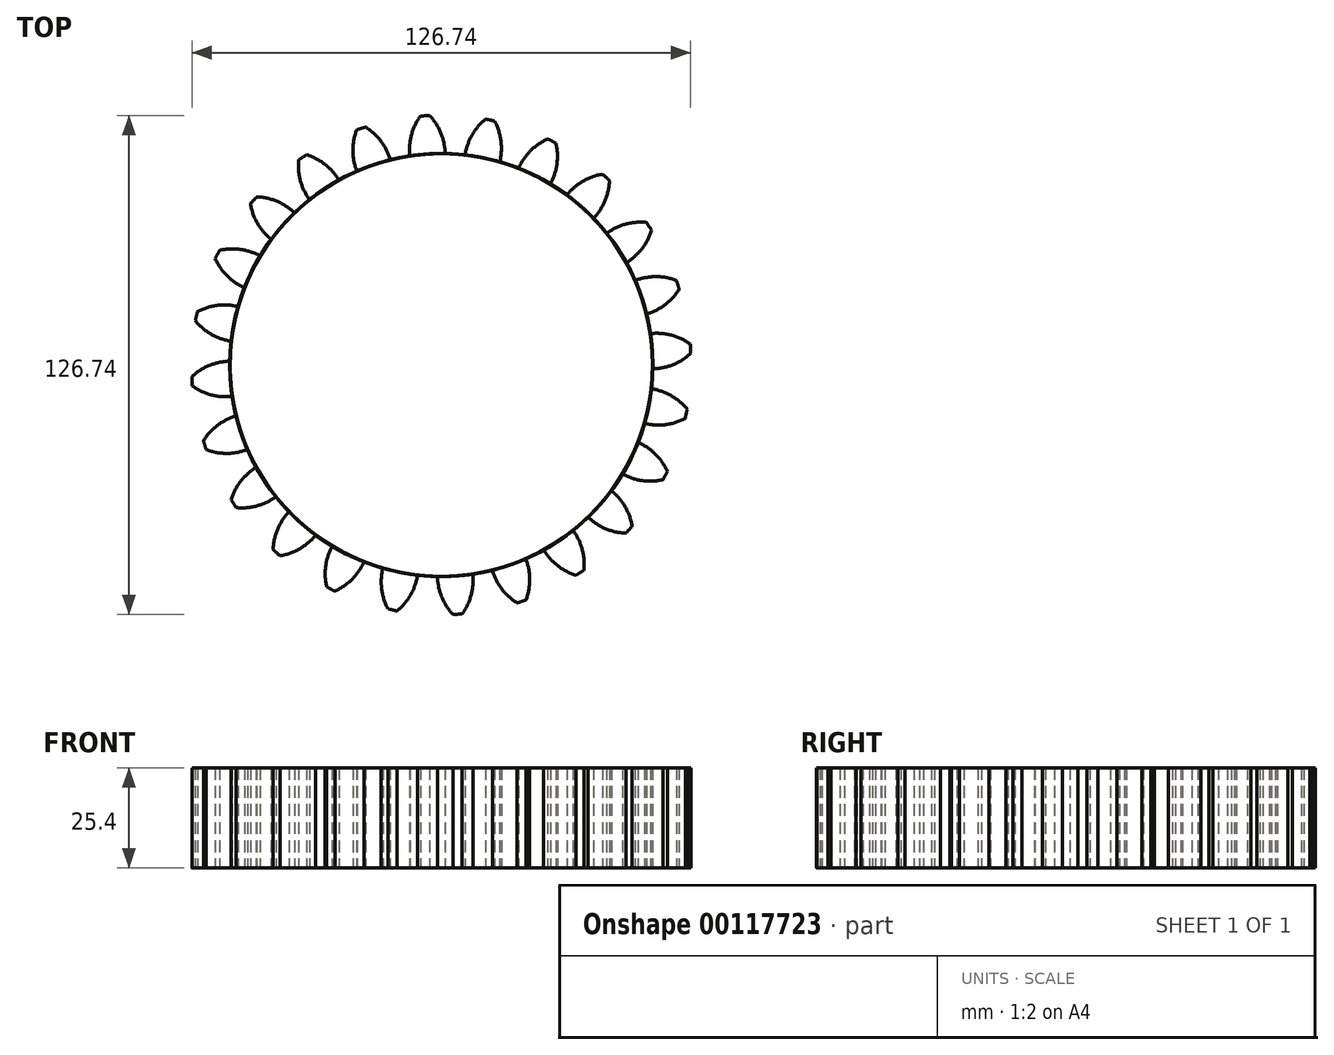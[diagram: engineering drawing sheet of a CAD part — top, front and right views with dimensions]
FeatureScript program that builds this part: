
annotation { "Feature Type Name" : "Feature", "Feature Type Description" : "" }
export const myFeature = defineFeature(function(context is Context, id is Id, definition is map)
    precondition{}
    {
        {
            var Q0;
            Q0=qCreatedBy(makeId("Top.planeOp"),FACE);
            var sketch = newSketch(context, id + "F0", { "sketchPlane" : qUnion([Q0])});
            skCircle(sketch, "E0", {"center": v(0, 0) * mm, "radius": 53.72 * mm});
            skCircle(sketch, "E1", {"center": v(0, 0) * mm, "radius": 58.67 * mm, "construction": true});
            skCircle(sketch, "E2", {"center": v(0, 0) * mm, "radius": 63.5 * mm, "construction": true});
            skLineSegment(sketch, "E3", {"start": v(0, 0) * mm, "end": v(0, 98.37) * mm, "construction": true});
            skLineSegment(sketch, "E4", {"start": v(0, 0) * mm, "end": v(-6.67, 101.74) * mm, "construction": true});
            skLineSegment(sketch, "E5", {"start": v(0, 58.67) * mm, "end": v(-58.76, 58.67) * mm, "construction": true});
            skLineSegment(sketch, "E6", {"start": v(0, 58.67) * mm, "end": v(-72.5, 32.29) * mm, "construction": true});
            skCircle(sketch, "E7", {"center": v(0, 58.67) * mm, "radius": 14.6 * mm, "construction": true});
            skCircle(sketch, "E8", {"center": v(0, 0) * mm, "radius": 55.14 * mm, "construction": true});
            skCircle(sketch, "E9", {"center": v(-13.62, 53.4) * mm, "radius": 14.6 * mm, "construction": true});
            skArc(sketch, "E10", {"start": v(0, 58.67) * mm, "mid": v(-1.27, 61.2) * mm, "end": v(-3, 63.43) * mm});
            skArc(sketch, "E11", {"start": v(0.98, 53.71) * mm, "mid": v(0.7, 56.23) * mm, "end": v(0, 58.67) * mm});
            skArc(sketch, "E12.MirrorCS", {"start": v(-7.99, 53.12) * mm, "mid": v(-8.04, 55.66) * mm, "end": v(-7.66, 58.17) * mm});
            skArc(sketch, "E13.MirrorCS", {"start": v(-7.66, 58.17) * mm, "mid": v(-6.72, 60.84) * mm, "end": v(-5.3, 63.28) * mm});
            skArc(sketch, "E14", {"start": v(-5.3, 63.28) * mm, "mid": v(-4.13, 63.32) * mm, "end": v(-2.95, 63.37) * mm});
            skSolve(sketch);
        }
        {
            var Q0;
            {var subQ0=sQuery(id+"F0.wireOp",EDGE,"E0");var subQ1=makeQuery(id+"F0.imprint","INTERSECT",VERTEX,{"derivedFrom":[subQ0,sQuery(id+"F0.wireOp",EDGE,"E11")]});Q0=makeQuery(id+"F0.imprint","IMPRINT",FACE,{"disambiguationData":[TD([[makeQuery(id+"F0.imprint","IMPRINT",EDGE,{"disambiguationData":[TD([[subQ1,-1.0]])],"derivedFrom":subQ0}),1.0]])]});}
            var Q1;
            {var subQ1=sQuery(id+"F0.wireOp",EDGE,"E11");Q1=makeQuery(id+"F0.imprint","IMPRINT",FACE,{"disambiguationData":[TD([[makeQuery(id+"F0.imprint","IMPRINT",EDGE,{"derivedFrom":subQ1}),1.0]])]});}
            extrude(context, id + "F1", {"entities" : qUnion([Q0, Q1]), "depth" : 25.4 * mm});
        }
        {
            var Q0;
            Q0=makeQuery(id+"F1.opExtrude","SWEPT_BODY",BODY,{"disambiguationData":[OSD([sQuery(id+"F0.wireOp",EDGE,"E0"),sQuery(id+"F0.wireOp",EDGE,"E10"),sQuery(id+"F0.wireOp",EDGE,"E11"),sQuery(id+"F0.wireOp",EDGE,"E12.MirrorCS"),sQuery(id+"F0.wireOp",EDGE,"E13.MirrorCS"),sQuery(id+"F0.wireOp",EDGE,"E14")])]});
            var Q1;
            Q1=makeQuery(id+"F1.opExtrude","SWEPT_FACE",FACE,{"disambiguationData":[OSD([sQuery(id+"F0.wireOp",EDGE,"E0")])]});
            circularPattern(context, id + "F2", {"entities" : qUnion([Q0]), "axis" : qUnion([Q1]), "angle" : 15 * degree, "instanceCount" : 24});
        }
    });
